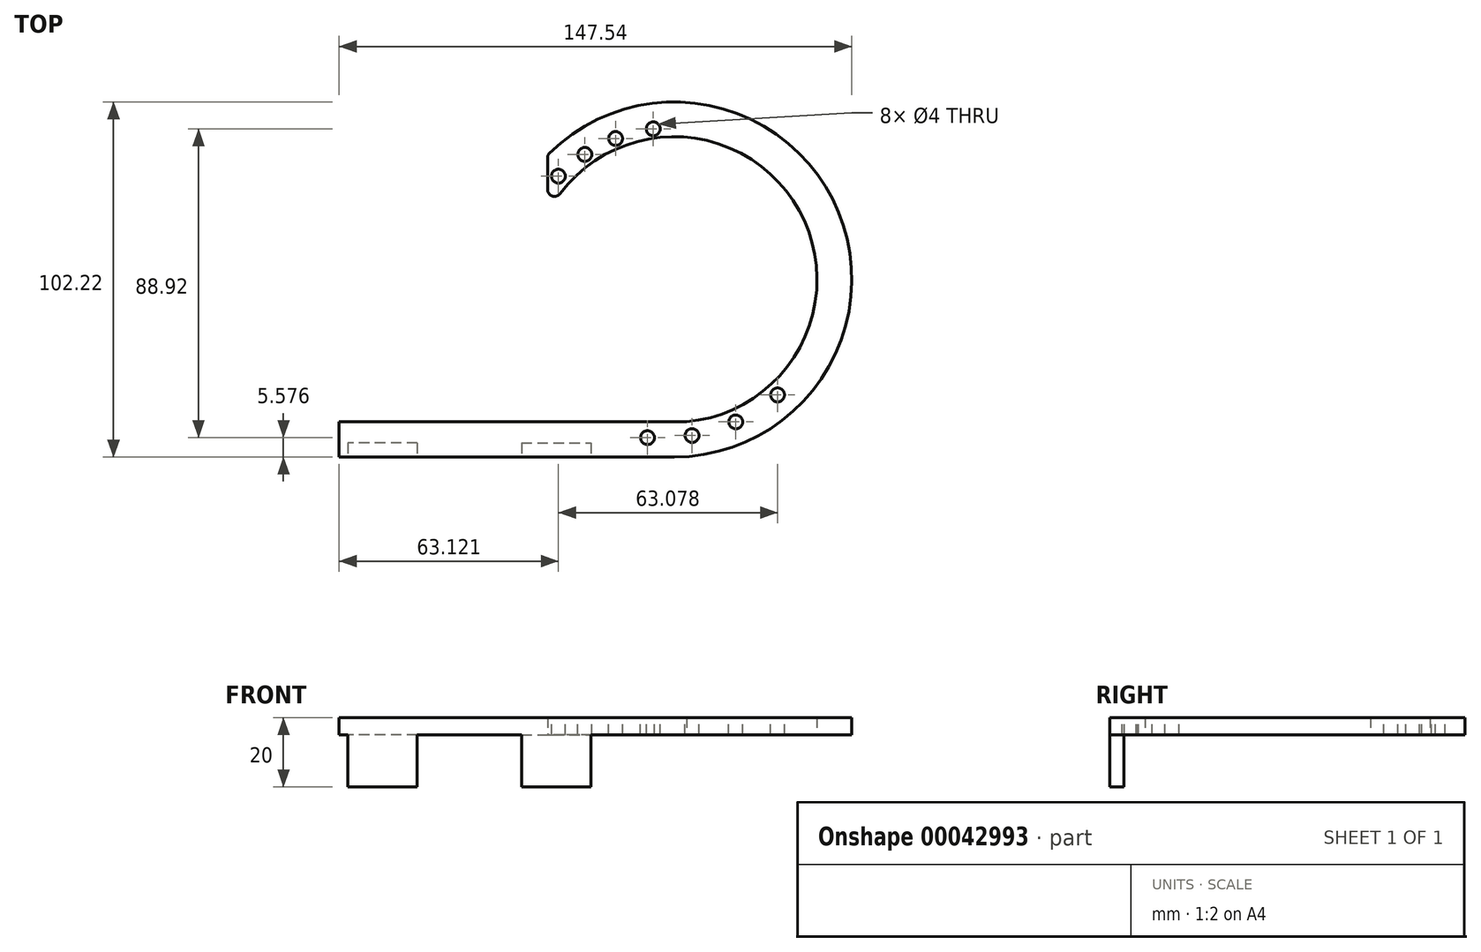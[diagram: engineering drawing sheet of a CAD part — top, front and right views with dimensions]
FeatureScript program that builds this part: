
annotation { "Feature Type Name" : "Feature", "Feature Type Description" : "" }
export const myFeature = defineFeature(function(context is Context, id is Id, definition is map)
    precondition{}
    {
        {
            var Q0;
            Q0=qCreatedBy(makeId("Top.planeOp"),FACE);
            var sketch = newSketch(context, id + "F0", { "sketchPlane" : qUnion([Q0])});
            skLineSegment(sketch, "E0.bottom", {"start": v(0, 10.15) * mm, "end": v(-100, 10.15) * mm});
            skLineSegment(sketch, "E0.top", {"start": v(-3.52, 0) * mm, "end": v(-100, 0) * mm});
            skLineSegment(sketch, "E0.right", {"start": v(-100, 10.15) * mm, "end": v(-100, 0) * mm});
            skArc(sketch, "E1", {"start": v(0, 10.15) * mm, "mid": v(30.64, 73.91) * mm, "end": v(-40, 70.15) * mm});
            skArc(sketch, "E2.0", {"start": v(-3.52, 0) * mm, "mid": v(43.56, 70.88) * mm, "end": v(-40, 86.96) * mm});
            skLineSegment(sketch, "E3", {"start": v(-40, 86.96) * mm, "end": v(-40, 70.15) * mm});
            skPoint(sketch, "E4", {"position": v(-100, 70.15) * mm});
            skSolve(sketch);
        }
        {
            var Q0;
            Q0=qSketchRegion(id+"F0",true);
            extrude(context, id + "F1", {"entities" : qUnion([Q0]), "depth" : 5 * mm});
        }
        {
            var Q0;
            Q0=makeQuery(id+"F1.opExtrude","SWEPT_EDGE",EDGE,{"disambiguationData":[OSD([sQuery(id+"F0.wireOp",EDGE,"E1"),sQuery(id+"F0.wireOp",EDGE,"E3")])]});
            var Q1;
            Q1=makeQuery(id+"F1.opExtrude","SWEPT_EDGE",EDGE,{"disambiguationData":[OSD([sQuery(id+"F0.wireOp",EDGE,"E2.0"),sQuery(id+"F0.wireOp",EDGE,"E3")])]});
            fillet(context, id + "F2", {"entities" : qUnion([Q0, Q1]), "radius" : 2 * mm, "tangentPropagation" : true, "allowEdgeOverflow" : false});
        }
        {
            var Q0;
            Q0=makeQuery(id+"F1.opExtrude","CAP_FACE",FACE,{"disambiguationData":[OSD([sQuery(id+"F0.wireOp",EDGE,"E0.bottom"),sQuery(id+"F0.wireOp",EDGE,"E0.top"),sQuery(id+"F0.wireOp",EDGE,"E0.right"),sQuery(id+"F0.wireOp",EDGE,"E1"),sQuery(id+"F0.wireOp",EDGE,"E2.0"),sQuery(id+"F0.wireOp",EDGE,"E3")])],"isStart":false});
            var sketch = newSketch(context, id + "F3", { "sketchPlane" : qUnion([Q0])});
            skCircle(sketch, "E5", {"center": v(-36.88, 80.88) * mm, "radius": 2 * mm});
            skCircle(sketch, "E6", {"center": v(-20.41, 91.71) * mm, "radius": 2 * mm});
            skCircle(sketch, "E7", {"center": v(-9.58, 94.5) * mm, "radius": 2 * mm});
            skArc(sketch, "E8", {"start": v(-9.58, 94.5) * mm, "mid": v(-24.36, 89.96) * mm, "end": v(-36.88, 80.88) * mm, "construction": true});
            skCircle(sketch, "E9", {"center": v(-29.29, 87.12) * mm, "radius": 2 * mm});
            skCircle(sketch, "E10", {"center": v(-11.24, 5.58) * mm, "radius": 2 * mm});
            skCircle(sketch, "E11", {"center": v(14.16, 10.1) * mm, "radius": 2 * mm});
            skCircle(sketch, "E12", {"center": v(26.2, 17.89) * mm, "radius": 2 * mm});
            skCircle(sketch, "E13", {"center": v(1.57, 6.17) * mm, "radius": 2 * mm});
            skArc(sketch, "E14", {"start": v(-11.24, 5.58) * mm, "mid": v(8.72, 7.96) * mm, "end": v(26.2, 17.89) * mm, "construction": true});
            skSolve(sketch);
        }
        {
            var Q0;
            Q0=qSketchRegion(id+"F3",true);
            extrude(context, id + "F4", {"entities" : qUnion([Q0]), "operationType" : NewBodyOperationType.REMOVE, "oppositeDirection" : true, "depth" : 5 * mm});
        }
        {
            var Q0;
            Q0=makeQuery(id+"F1.opExtrude","CAP_FACE",FACE,{"disambiguationData":[OSD([sQuery(id+"F0.wireOp",EDGE,"E0.bottom"),sQuery(id+"F0.wireOp",EDGE,"E0.top"),sQuery(id+"F0.wireOp",EDGE,"E0.right"),sQuery(id+"F0.wireOp",EDGE,"E1"),sQuery(id+"F0.wireOp",EDGE,"E2.0"),sQuery(id+"F0.wireOp",EDGE,"E3")])],"isStart":false});
            var sketch = newSketch(context, id + "F5", { "sketchPlane" : qUnion([Q0])});
            skLineSegment(sketch, "E15.right", {"start": v(-27.5, 4) * mm, "end": v(-27.5, 0) * mm});
            skLineSegment(sketch, "E16", {"start": v(-47.5, 4) * mm, "end": v(-47.5, 0) * mm});
            skLineSegment(sketch, "E17", {"start": v(-77.5, 4) * mm, "end": v(-77.5, 0) * mm});
            skLineSegment(sketch, "E18", {"start": v(-47.5, 4) * mm, "end": v(-27.5, 4) * mm});
            skLineSegment(sketch, "E19", {"start": v(-47.5, 0) * mm, "end": v(-27.5, 0) * mm});
            skLineSegment(sketch, "E20", {"start": v(-77.5, 4) * mm, "end": v(-97.5, 4) * mm});
            skLineSegment(sketch, "E21", {"start": v(-77.5, 0) * mm, "end": v(-97.5, 0) * mm});
            skLineSegment(sketch, "E22", {"start": v(-97.5, 4) * mm, "end": v(-97.5, 0) * mm});
            skSolve(sketch);
        }
        {
            var Q0;
            Q0=qSketchRegion(id+"F5",true);
            extrude(context, id + "F6", {"entities" : qUnion([Q0]), "operationType" : NewBodyOperationType.ADD, "oppositeDirection" : true, "depth" : 20 * mm});
        }
    });
